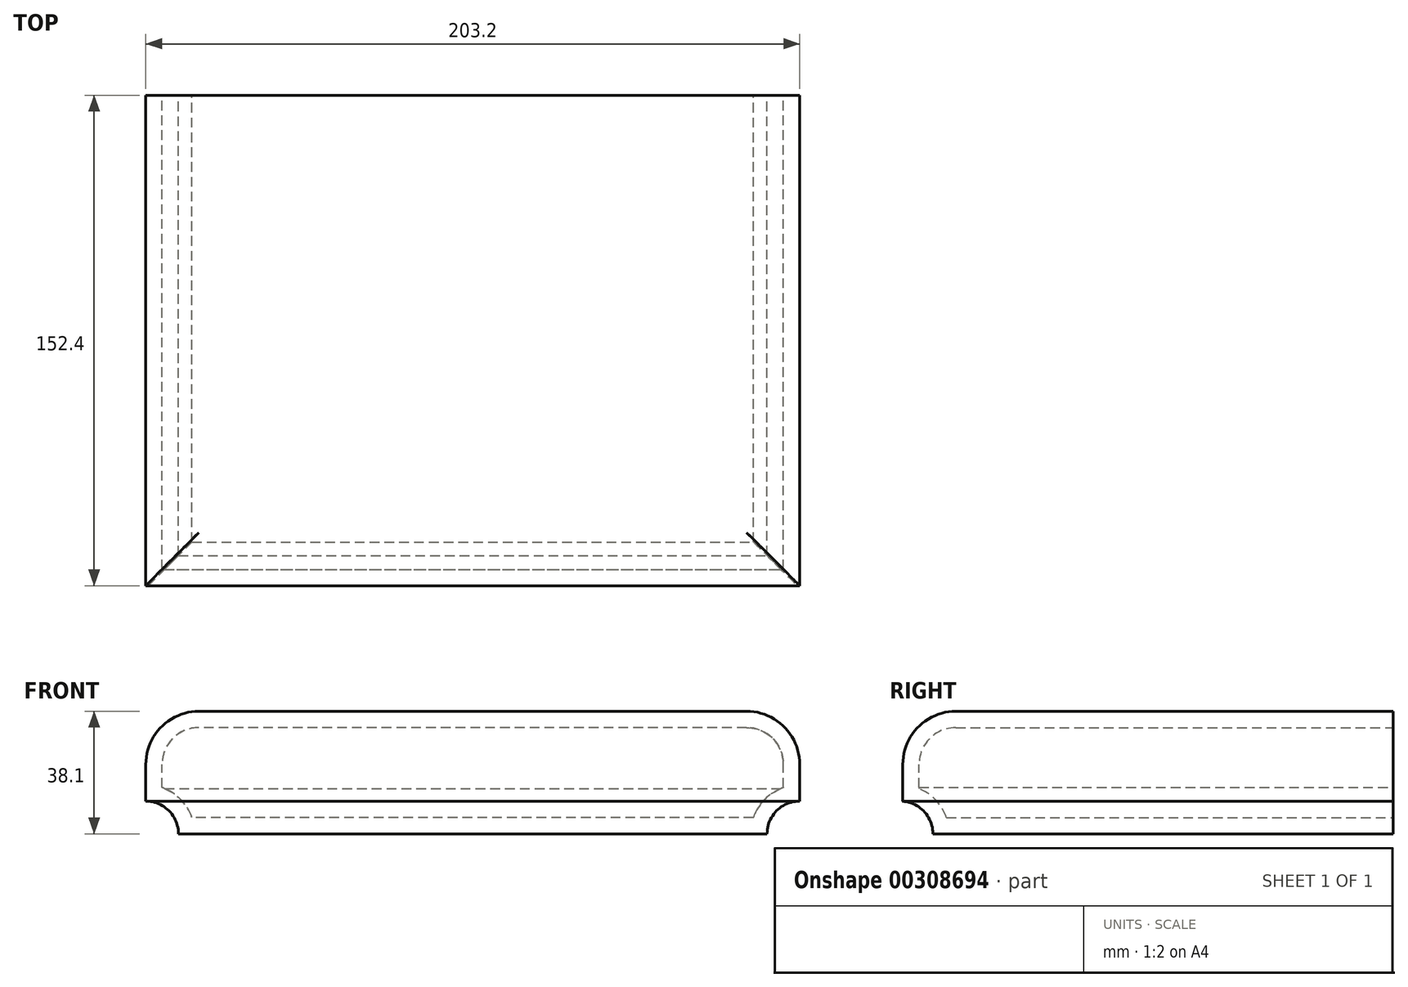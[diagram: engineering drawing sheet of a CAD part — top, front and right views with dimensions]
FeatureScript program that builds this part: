
annotation { "Feature Type Name" : "Feature", "Feature Type Description" : "" }
export const myFeature = defineFeature(function(context is Context, id is Id, definition is map)
    precondition{}
    {
        {
            var Q0;
            Q0=qCreatedBy(makeId("Front.planeOp"),FACE);
            var sketch = newSketch(context, id + "F0", { "sketchPlane" : qUnion([Q0])});
            skLineSegment(sketch, "E0.bottom", {"start": v(-10.16, 0) * mm, "end": v(-193.04, 0) * mm});
            skLineSegment(sketch, "E0.top", {"start": v(0, 38.1) * mm, "end": v(-203.2, 38.1) * mm});
            skLineSegment(sketch, "E0.left", {"start": v(0, 10.16) * mm, "end": v(0, 38.1) * mm});
            skLineSegment(sketch, "E0.right", {"start": v(-203.2, 10.16) * mm, "end": v(-203.2, 38.1) * mm});
            skArc(sketch, "E1", {"start": v(0, 10.16) * mm, "mid": v(-7.18, 7.18) * mm, "end": v(-10.16, 0) * mm});
            skArc(sketch, "E2", {"start": v(-193.04, 0) * mm, "mid": v(-196.02, 7.18) * mm, "end": v(-203.2, 10.16) * mm});
            skSolve(sketch);
        }
        {
            var Q0;
            Q0=makeQuery(id+"F0.imprint","IMPRINT",FACE,{"disambiguationData":[TD([[makeQuery(id+"F0.imprint","IMPRINT",EDGE,{"derivedFrom":sQuery(id+"F0.wireOp",EDGE,"E0.bottom")}),-1.0]])]});
            extrude(context, id + "F5", {"entities" : qUnion([Q0]), "depth" : 152.4 * mm});
        }
        {
            var Q0;
            Q0=makeQuery(id+"F5.opExtrude","SWEPT_FACE",FACE,{"disambiguationData":[OSD([sQuery(id+"F0.wireOp",EDGE,"E0.left")])]});
            var sketch = newSketch(context, id + "F1", { "sketchPlane" : qUnion([Q0])});
            skCircle(sketch, "E3", {"center": v(-153.18, 0) * mm, "radius": 10.16 * mm});
            skSolve(sketch);
        }
        {
            var Q0;
            Q0=qSketchRegion(id+"F1",true);
            extrude(context, id + "F2", {"entities" : qUnion([Q0]), "operationType" : NewBodyOperationType.REMOVE, "oppositeDirection" : true, "depth" : 254 * mm});
        }
        {
            var Q0;
            Q0=makeQuery(id+"F5.opExtrude","CAP_EDGE",EDGE,{"disambiguationData":[OSD([sQuery(id+"F0.wireOp",EDGE,"E0.top")])],"isStart":false});
            var Q1;
            Q1=makeQuery(id+"F5.opExtrude","SWEPT_EDGE",EDGE,{"disambiguationData":[OSD([sQuery(id+"F0.wireOp",EDGE,"E0.top"),sQuery(id+"F0.wireOp",EDGE,"E0.right")])]});
            var Q2;
            Q2=makeQuery(id+"F5.opExtrude","SWEPT_EDGE",EDGE,{"disambiguationData":[OSD([sQuery(id+"F0.wireOp",EDGE,"E0.top"),sQuery(id+"F0.wireOp",EDGE,"E0.left")])]});
            fillet(context, id + "F3", {"entities" : qUnion([Q0, Q1, Q2]), "radius" : 16.5 * mm, "tangentPropagation" : true, "allowEdgeOverflow" : false});
        }
        {
            var Q0;
            Q0=makeQuery(id+"F5.opExtrude","CAP_FACE",FACE,{"disambiguationData":[OSD([sQuery(id+"F0.wireOp",EDGE,"E0.bottom"),sQuery(id+"F0.wireOp",EDGE,"E0.top"),sQuery(id+"F0.wireOp",EDGE,"E0.left"),sQuery(id+"F0.wireOp",EDGE,"E0.right"),sQuery(id+"F0.wireOp",EDGE,"E1"),sQuery(id+"F0.wireOp",EDGE,"E2")])],"isStart":true});
            shell(context, id + "F6", {"entities" : qUnion([Q0]), "thickness" : 5.08 * mm});
        }
    });
